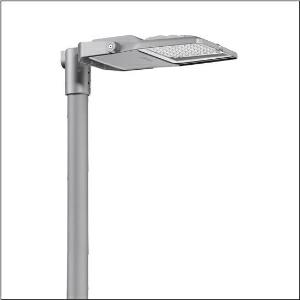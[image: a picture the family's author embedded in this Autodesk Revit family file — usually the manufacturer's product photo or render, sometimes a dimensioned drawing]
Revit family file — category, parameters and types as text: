
# Revit family: floodlight_fl_21_iq_mini___pl33t_5xa7771c2f3a_7d89
name_source: partatom
category: Lighting Fixtures
units: mm (PartAtom-declared; Revit-internal decimal feet)

## family parameters
Cut with Voids When Loaded = No
Host = Face
Light Source = No
Part Type = Normal
Room Calculation Point = No
Round Connector Dimension = Use Diameter
Shared = No

## types (1)
- --- (1 x LED, 12060 lm, 87.2 W, 3000K)
    Apparent Load = 87 VA
    CIE Flux Codes = 26 75 99 100 100
    Color Rendering = 70
    Color Temperature = 3000K
    Default Elevation = 1800 mm
    Description = Floodlight FL 21 iQ mini, floodlight, primary light control with lens, of PMMA, primary optical cover: protective disc, of toughened safety glass, transparent, light distribution: PL33T, light emission: direct distribution, installation type: surface-mounted, LED, High Power LED, rated luminous flux: 12.060lm, luminous efficacy: 138lm/W, light colour: 730, colour temperature: 3000K, control: Auto-Match, Temp-Guard, Lumen-Switch, Night-Set, Smart-Wire, Light-Fading, Desk-Remote (wireless, voltage-free reading and setting of iQ features in the workshop via application-optimized NFC function/RFID function), optimised constant luminous flux control (CLO 2.0), with terminal, 6-pole, mains connection: 220..240V, AC, 50/60Hz, start of lifetime: 87W, end of service life: 92W, reduction: 40W, luminaire housing, of diecast aluminium, powder-coated, Siteco® metallic grey (DB 702S), corrosivity category C5 mid according to DIN EN ISO 12944, sealing non-destructively replaceable, please order mast flange separately, mast bracket, of steel, galvanised, powder-coated, Siteco® metallic grey (DB 702S), protection rating (complete): IP66, insulation class (complete): insulation class II (safety insulation), certification: CE, ENEC, VDE, protection symbol: D, impact resistance: IK08, permissible operating ambient temperature: -40..+40°C, permissible operating ambient temperature for outdoor applications: -40..+50°C, standard: DIN EN 12944, LABS conformity tested according to VDMA 24364:2018-05, packaging unit: 1 piece

Light Distribution: PL33T
    Height = 70 mm
    Lamp = 1 x LED
    Lamp Light Flux = 12060 lm
    Lamp Power = 87.2 W
    Lamp count = 1
    Length = 485 mm
    Luminous efficacy = 138 lm/W
    Manufacturer = Siteco
    ModVariant = No
    Model = 5XA7771C2F3A
    Number of Poles = 1
    OnlyDefault = Yes
    Power Factor = 1
    Product Name = Floodlight FL 21 iQ mini | PL33T
    Product group = floodlight | pylon annexe
    ProductGroupID = 6200
    Protection Class = Protection class II
    Protection Degree = IP 66
    RLX_Detail_Level = 1
    RLX_Emergency_Light_Flux = 0 lm
    RLX_Emergency_Type = 0
    RLX_Emergency_Type_DB = No
    RlxData = <blob elided: 101225 chars, md5=7eeb5ecc>
    Socket = socket
    Standby Power = 0 W
    System Light Flux = 12060 lm
    System Power = 87 W
    Type Comments = factory setting: luminous flux: 100 % | dim-lin: 254 | 456 mA
    Type Image = l_1007125.jpg
    URL = http://relux.com
    VarID = @adj_082227
    Voltage = 0 V
    Weight = 0.00 kg
    Width = 337 mm

## geometry (parser evidence)
native form markers: Blend x4, Sweep x12
no freeform markers — native parametric forms only
